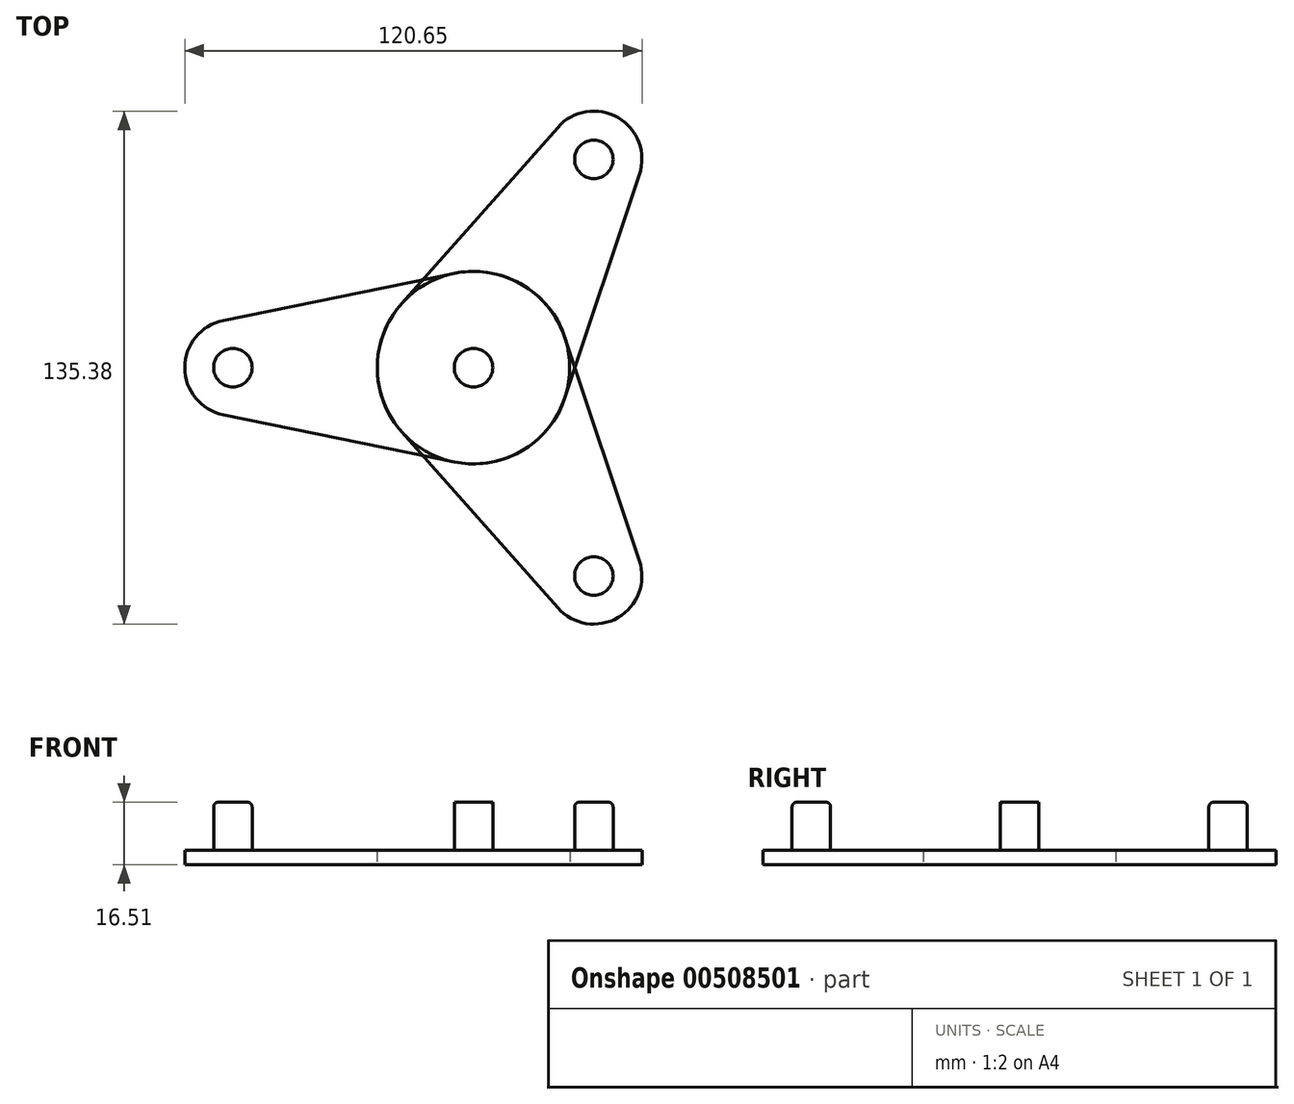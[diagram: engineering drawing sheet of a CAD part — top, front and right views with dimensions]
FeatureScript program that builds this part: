
annotation { "Feature Type Name" : "Feature", "Feature Type Description" : "" }
export const myFeature = defineFeature(function(context is Context, id is Id, definition is map)
    precondition{}
    {
        {
            var Q0;
            Q0=qCreatedBy(makeId("Top.planeOp"),FACE);
            var sketch = newSketch(context, id + "F0", { "sketchPlane" : qUnion([Q0])});
            skCircle(sketch, "E0", {"center": v(0, 0) * mm, "radius": 25.4 * mm});
            skCircle(sketch, "E1", {"center": v(0, 0) * mm, "radius": 6.35 * mm});
            skLineSegment(sketch, "E2", {"start": v(0, 0) * mm, "end": v(-63.5, 0) * mm, "construction": true});
            skCircle(sketch, "E3", {"center": v(-63.5, 0) * mm, "radius": 12.7 * mm});
            skLineSegment(sketch, "E4", {"start": v(-5.08, 24.89) * mm, "end": v(-66.04, 12.44) * mm});
            skLineSegment(sketch, "E5.MirrorCS", {"start": v(-5.08, -24.89) * mm, "end": v(-66.04, -12.44) * mm});
            skCircle(sketch, "E6", {"center": v(-63.5, 0) * mm, "radius": 6.35 * mm});
            skSolve(sketch);
        }
        {
            var Q0;
            Q0=makeQuery(id+"F0.imprint","IMPRINT",FACE,{"disambiguationData":[TD([[makeQuery(id+"F0.imprint","IMPRINT",EDGE,{"derivedFrom":sQuery(id+"F0.wireOp",EDGE,"E6")}),-1.0]])]});
            var Q1;
            Q1=makeQuery(id+"F0.imprint","IMPRINT",FACE,{"disambiguationData":[TD([[makeQuery(id+"F0.imprint","IMPRINT",EDGE,{"derivedFrom":sQuery(id+"F0.wireOp",EDGE,"E1")}),-1.0]])]});
            var Q2;
            {var subQ0=sQuery(id+"F0.wireOp",EDGE,"E4");Q2=makeQuery(id+"F0.imprint","IMPRINT",FACE,{"disambiguationData":[TD([[makeQuery(id+"F0.imprint","IMPRINT",EDGE,{"derivedFrom":subQ0}),1.0]])]});}
            var Q3;
            Q3=makeQuery(id+"F0.imprint","IMPRINT",FACE,{"disambiguationData":[TD([[makeQuery(id+"F0.imprint","IMPRINT",EDGE,{"derivedFrom":sQuery(id+"F0.wireOp",EDGE,"E6")}),1.0]])]});
            var Q4;
            Q4=makeQuery(id+"F0.imprint","IMPRINT",FACE,{"disambiguationData":[TD([[makeQuery(id+"F0.imprint","IMPRINT",EDGE,{"derivedFrom":sQuery(id+"F0.wireOp",EDGE,"E1")}),1.0]])]});
            extrude(context, id + "F1", {"entities" : qUnion([Q0, Q1, Q2, Q3, Q4]), "depth" : 3.8 * mm});
        }
        {
            var Q0;
            Q0=makeQuery(id+"F1.opExtrude","CAP_FACE",FACE,{"disambiguationData":[OSD([sQuery(id+"F0.wireOp",EDGE,"E0"),sQuery(id+"F0.wireOp",EDGE,"E3"),sQuery(id+"F0.wireOp",EDGE,"E4"),sQuery(id+"F0.wireOp",EDGE,"E5.MirrorCS")])],"isStart":false});
            var sketch = newSketch(context, id + "F2", { "sketchPlane" : qUnion([Q0])});
            skCircle(sketch, "E7", {"center": v(0, 0) * mm, "radius": 5.08 * mm});
            skCircle(sketch, "E8", {"center": v(-63.5, 0) * mm, "radius": 5.08 * mm});
            skSolve(sketch);
        }
        {
            var Q0;
            Q0=makeQuery(id+"F2.imprint","IMPRINT",FACE,{"disambiguationData":[TD([[makeQuery(id+"F2.imprint","IMPRINT",EDGE,{"derivedFrom":sQuery(id+"F2.wireOp",EDGE,"E8")}),1.0]])]});
            var Q1;
            Q1=makeQuery(id+"F2.imprint","IMPRINT",FACE,{"disambiguationData":[TD([[makeQuery(id+"F2.imprint","IMPRINT",EDGE,{"derivedFrom":sQuery(id+"F2.wireOp",EDGE,"E7")}),1.0]])]});
            extrude(context, id + "F3", {"entities" : qUnion([Q0, Q1]), "operationType" : NewBodyOperationType.ADD, "depth" : 12.7 * mm});
        }
        {
            var Q0;
            Q0=qCreatedBy(makeId("Right.planeOp"),FACE);
            var sketch = newSketch(context, id + "F4", { "sketchPlane" : qUnion([Q0])});
            skLineSegment(sketch, "E9", {"start": v(0, 0) * mm, "end": v(0, -16.8) * mm, "construction": true});
            skSolve(sketch);
        }
        {
            var Q0;
            Q0=makeQuery(id+"F1.opExtrude","SWEPT_BODY",BODY,{"disambiguationData":[OSD([sQuery(id+"F0.wireOp",EDGE,"E0"),sQuery(id+"F0.wireOp",EDGE,"E3"),sQuery(id+"F0.wireOp",EDGE,"E4"),sQuery(id+"F0.wireOp",EDGE,"E5.MirrorCS")])]});
            var Q1;
            Q1=sQuery(id+"F4.wireOp",EDGE,"E9");
            circularPattern(context, id + "F5", {"entities" : qUnion([Q0]), "axis" : qUnion([Q1]), "angle" : 360 * degree, "instanceCount" : 3, "equalSpace" : true});
        }
        {
            var Q0;
            Q0=makeQuery(id+"F3.opExtrude","CAP_EDGE",EDGE,{"disambiguationData":[OSD([sQuery(id+"F2.wireOp",EDGE,"E8")])],"isStart":false});
            var Q1;
            Q1=makeQuery(id+"F3.opExtrude","CAP_EDGE",EDGE,{"disambiguationData":[OSD([sQuery(id+"F2.wireOp",EDGE,"E7")])],"isStart":false});
            var Q2;
            Q2=makeQuery(id+"F5.opPattern","COPY",EDGE,{"derivedFrom":makeQuery(id+"F3.opExtrude","CAP_EDGE",EDGE,{"disambiguationData":[OSD([sQuery(id+"F2.wireOp",EDGE,"E8")])],"isStart":false}),"instanceName":"2"});
            var Q3;
            Q3=makeQuery(id+"F5.opPattern","COPY",EDGE,{"derivedFrom":makeQuery(id+"F3.opExtrude","CAP_EDGE",EDGE,{"disambiguationData":[OSD([sQuery(id+"F2.wireOp",EDGE,"E8")])],"isStart":false}),"instanceName":"1"});
            fillet(context, id + "F6", {"entities" : qUnion([Q0, Q1, Q2, Q3]), "radius" : 1.27 * mm, "tangentPropagation" : true, "allowEdgeOverflow" : false});
        }
    });
